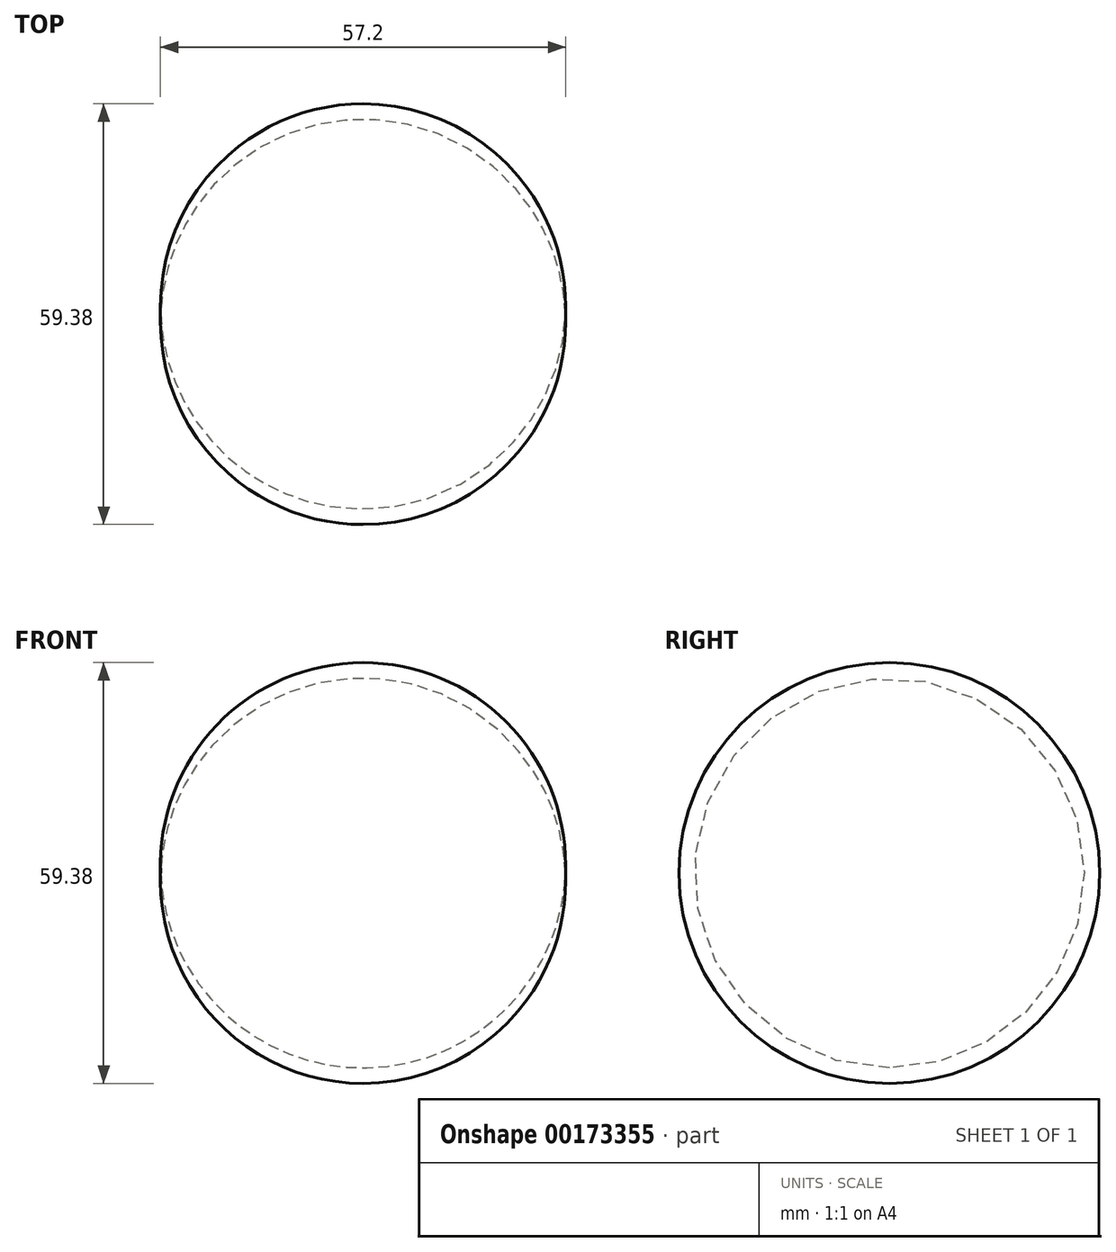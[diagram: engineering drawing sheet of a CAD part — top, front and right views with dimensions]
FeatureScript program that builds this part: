
annotation { "Feature Type Name" : "Feature", "Feature Type Description" : "" }
export const myFeature = defineFeature(function(context is Context, id is Id, definition is map)
    precondition{}
    {
        {
            var Q0;
            Q0=qCreatedBy(makeId("Front.planeOp"),FACE);
            var sketch = newSketch(context, id + "F0", { "sketchPlane" : qUnion([Q0])});
            skArc(sketch, "E0", {"start": v(29.92, 0) * mm, "mid": v(1.35, 27.5) * mm, "end": v(-27.23, 0) * mm});
            skLineSegment(sketch, "E1", {"start": v(-27.23, 0) * mm, "end": v(29.92, 0) * mm});
            skSolve(sketch);
        }
        {
            var Q0;
            Q0=makeQuery(id+"F0.imprint","IMPRINT",FACE,{"disambiguationData":[TD([[makeQuery(id+"F0.imprint","IMPRINT",EDGE,{"derivedFrom":sQuery(id+"F0.wireOp",EDGE,"E0")}),1.0]])]});
            var Q1;
            Q1=sQuery(id+"F0.wireOp",EDGE,"E0");
            var Q2;
            Q2=sQuery(id+"F0.wireOp",EDGE,"E1");
            revolve(context, id + "F1", {"entities" : qUnion([Q0]), "surfaceEntities" : qUnion([Q1]), "axis" : qUnion([Q2]), "revolveType" : RevolveType.FULL});
        }
    });
